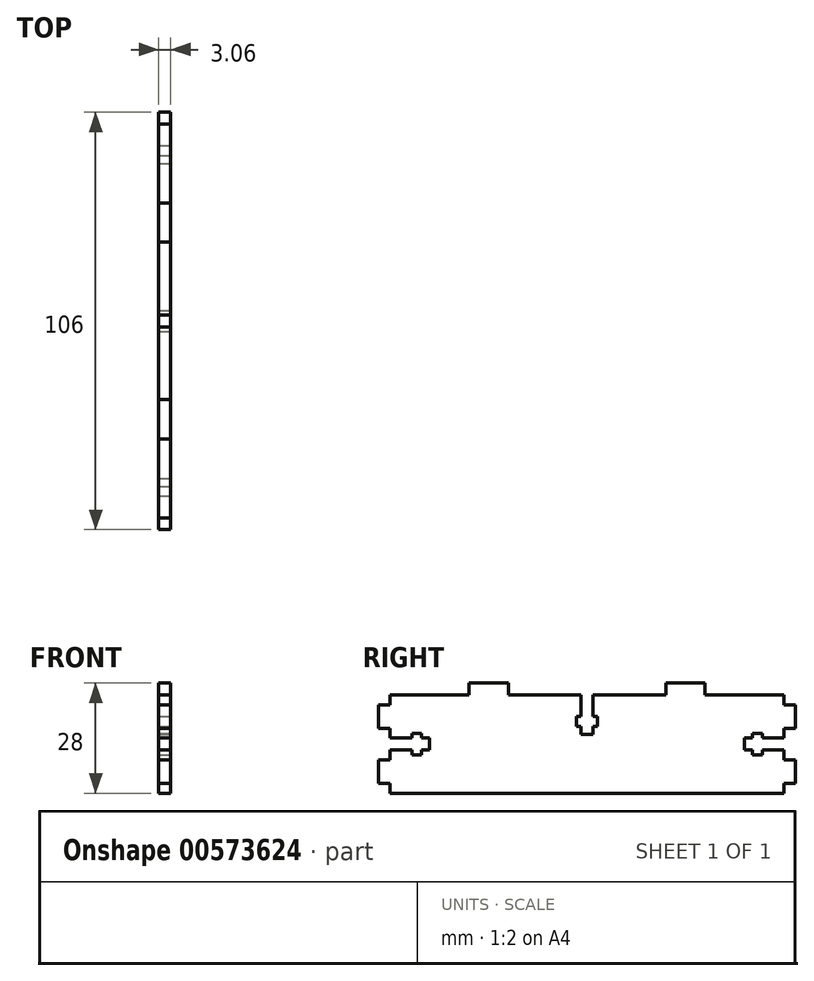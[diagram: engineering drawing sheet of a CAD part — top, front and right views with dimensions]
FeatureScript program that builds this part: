
annotation { "Feature Type Name" : "Feature", "Feature Type Description" : "" }
export const myFeature = defineFeature(function(context is Context, id is Id, definition is map)
    precondition{}
    {
        {
            var Q0;
            Q0=qCreatedBy(makeId("Right.planeOp"),FACE);
            var sketch = newSketch(context, id + "F0", { "sketchPlane" : qUnion([Q0])});
            skLineSegment(sketch, "E0.bottom", {"start": v(50, -12.5) * mm, "end": v(-50, -12.5) * mm});
            skLineSegment(sketch, "E0.top", {"start": v(50, 12.5) * mm, "end": v(-50, 12.5) * mm});
            skLineSegment(sketch, "E0.left", {"start": v(50, -12.5) * mm, "end": v(50, 12.5) * mm});
            skLineSegment(sketch, "E0.right", {"start": v(-50, -12.5) * mm, "end": v(-50, 12.5) * mm});
            skPoint(sketch, "E0.middle", {"position": v(0, 0) * mm});
            skSolve(sketch);
        }
        {
            var Q0;
            Q0 = qSketchRegion(id + "F0", true);
            extrude(context, id + "F1", {"entities" : qUnion([Q0]), "endBound" : BoundingType.SYMMETRIC, "depth" : 3.05 * mm, "offsetDistance" : 25 * mm});
        }
        {
            var Q0;
            Q0=makeQuery(id+"F1.opExtrude","CAP_FACE",FACE,{"disambiguationData":[OSD([sQuery(id+"F0.wireOp",EDGE,"E0.bottom"),sQuery(id+"F0.wireOp",EDGE,"E0.top"),sQuery(id+"F0.wireOp",EDGE,"E0.left"),sQuery(id+"F0.wireOp",EDGE,"E0.right")])],"isStart":false});
            var sketch = newSketch(context, id + "F2", { "sketchPlane" : qUnion([Q0])});
            skLineSegment(sketch, "E1", {"start": v(0, 12.5) * mm, "end": v(0, -12.5) * mm, "construction": true});
            skLineSegment(sketch, "E2", {"start": v(-50, 0) * mm, "end": v(50, 0) * mm, "construction": true});
            skLineSegment(sketch, "E3.bottom", {"start": v(-50, 10) * mm, "end": v(-53, 10) * mm});
            skLineSegment(sketch, "E3.top", {"start": v(-50, 4) * mm, "end": v(-53, 4) * mm});
            skLineSegment(sketch, "E3.left", {"start": v(-50, 10) * mm, "end": v(-50, 4) * mm});
            skLineSegment(sketch, "E3.right", {"start": v(-53, 10) * mm, "end": v(-53, 4) * mm});
            skLineSegment(sketch, "E4.MirrorCS", {"start": v(-53, -10) * mm, "end": v(-53, -4) * mm});
            skLineSegment(sketch, "E5.MirrorCS", {"start": v(-50, -10) * mm, "end": v(-50, -4) * mm});
            skLineSegment(sketch, "E6.MirrorCS", {"start": v(-50, -10) * mm, "end": v(-53, -10) * mm});
            skLineSegment(sketch, "E7.MirrorCS", {"start": v(-50, -4) * mm, "end": v(-53, -4) * mm});
            skLineSegment(sketch, "E8.MirrorCS", {"start": v(53, -10) * mm, "end": v(53, -4) * mm});
            skLineSegment(sketch, "E9.MirrorCS", {"start": v(53, 10) * mm, "end": v(53, 4) * mm});
            skLineSegment(sketch, "E10.MirrorCS", {"start": v(50, 10) * mm, "end": v(50, 4) * mm});
            skLineSegment(sketch, "E11.MirrorCS", {"start": v(50, 4) * mm, "end": v(53, 4) * mm});
            skLineSegment(sketch, "E12.MirrorCS", {"start": v(50, 10) * mm, "end": v(53, 10) * mm});
            skLineSegment(sketch, "E13.MirrorCS", {"start": v(50, -10) * mm, "end": v(50, -4) * mm});
            skLineSegment(sketch, "E14.MirrorCS", {"start": v(50, -4) * mm, "end": v(53, -4) * mm});
            skLineSegment(sketch, "E15.MirrorCS", {"start": v(50, -10) * mm, "end": v(53, -10) * mm});
            skSolve(sketch);
        }
        {
            var Q0;
            Q0 = qSketchRegion(id + "F2", true);
            var Q1;
            Q1=makeQuery(id+"F1.opExtrude","CAP_FACE",FACE,{"disambiguationData":[OSD([sQuery(id+"F0.wireOp",EDGE,"E0.bottom"),sQuery(id+"F0.wireOp",EDGE,"E0.top"),sQuery(id+"F0.wireOp",EDGE,"E0.left"),sQuery(id+"F0.wireOp",EDGE,"E0.right")])],"isStart":true});
            extrude(context, id + "F3", {"entities" : qUnion([Q0]), "operationType" : NewBodyOperationType.ADD, "endBound" : BoundingType.UP_TO_SURFACE, "oppositeDirection" : true, "depth" : 3.05 * mm, "endBoundEntityFace" : qUnion([Q1]), "offsetDistance" : 25 * mm});
        }
        {
            var Q0;
            Q0=makeQuery(id+"F3.boolean.opBoolean","MERGE",FACE,{"derivedFrom":[makeQuery(id+"F1.opExtrude","CAP_FACE",FACE,{"disambiguationData":[OSD([sQuery(id+"F0.wireOp",EDGE,"E0.bottom"),sQuery(id+"F0.wireOp",EDGE,"E0.top"),sQuery(id+"F0.wireOp",EDGE,"E0.left"),sQuery(id+"F0.wireOp",EDGE,"E0.right")])],"isStart":false}),makeQuery(id+"F3.opExtrude","CAP_FACE",FACE,{"disambiguationData":[OSD([sQuery(id+"F2.wireOp",EDGE,"E3.bottom"),sQuery(id+"F2.wireOp",EDGE,"E3.top"),sQuery(id+"F2.wireOp",EDGE,"E3.left"),sQuery(id+"F2.wireOp",EDGE,"E3.right")])],"isStart":true}),makeQuery(id+"F3.opExtrude","CAP_FACE",FACE,{"disambiguationData":[OSD([sQuery(id+"F2.wireOp",EDGE,"E4.MirrorCS"),sQuery(id+"F2.wireOp",EDGE,"E5.MirrorCS"),sQuery(id+"F2.wireOp",EDGE,"E6.MirrorCS"),sQuery(id+"F2.wireOp",EDGE,"E7.MirrorCS")])],"isStart":true}),makeQuery(id+"F3.opExtrude","CAP_FACE",FACE,{"disambiguationData":[OSD([sQuery(id+"F2.wireOp",EDGE,"E8.MirrorCS"),sQuery(id+"F2.wireOp",EDGE,"E13.MirrorCS"),sQuery(id+"F2.wireOp",EDGE,"E14.MirrorCS"),sQuery(id+"F2.wireOp",EDGE,"E15.MirrorCS")])],"isStart":true}),makeQuery(id+"F3.opExtrude","CAP_FACE",FACE,{"disambiguationData":[OSD([sQuery(id+"F2.wireOp",EDGE,"E9.MirrorCS"),sQuery(id+"F2.wireOp",EDGE,"E10.MirrorCS"),sQuery(id+"F2.wireOp",EDGE,"E11.MirrorCS"),sQuery(id+"F2.wireOp",EDGE,"E12.MirrorCS")])],"isStart":true})]});
            var sketch = newSketch(context, id + "F4", { "sketchPlane" : qUnion([Q0])});
            skLineSegment(sketch, "E16", {"start": v(-50, 0) * mm, "end": v(50, 0) * mm, "construction": true});
            skLineSegment(sketch, "E17.bottom", {"start": v(-1.55, 12.5) * mm, "end": v(1.55, 12.5) * mm});
            skLineSegment(sketch, "E17.top", {"start": v(-1.55, 2.5) * mm, "end": v(1.55, 2.5) * mm});
            skLineSegment(sketch, "E17.left", {"start": v(-1.55, 12.5) * mm, "end": v(-1.55, 2.5) * mm});
            skLineSegment(sketch, "E17.right", {"start": v(1.55, 12.5) * mm, "end": v(1.55, 2.5) * mm});
            skLineSegment(sketch, "E18", {"start": v(0, 12.5) * mm, "end": v(0, -12.5) * mm, "construction": true});
            skPoint(sketch, "E19", {"position": v(0, 2.5) * mm});
            skLineSegment(sketch, "E20", {"start": v(0, 12.5) * mm, "end": v(0, 2.5) * mm, "construction": true});
            skLineSegment(sketch, "E21.bottom", {"start": v(2.7, 4.5) * mm, "end": v(-2.7, 4.5) * mm});
            skLineSegment(sketch, "E21.top", {"start": v(2.7, 7) * mm, "end": v(-2.7, 7) * mm});
            skLineSegment(sketch, "E21.left", {"start": v(2.7, 4.5) * mm, "end": v(2.7, 7) * mm});
            skLineSegment(sketch, "E21.right", {"start": v(-2.7, 4.5) * mm, "end": v(-2.7, 7) * mm});
            skPoint(sketch, "E21.middle", {"position": v(0, 5.75) * mm});
            skLineSegment(sketch, "E22.bottom", {"start": v(-50, -1.55) * mm, "end": v(-50, 1.55) * mm});
            skLineSegment(sketch, "E22.top", {"start": v(-40, -1.55) * mm, "end": v(-40, 1.55) * mm});
            skLineSegment(sketch, "E22.left", {"start": v(-50, -1.55) * mm, "end": v(-40, -1.55) * mm});
            skLineSegment(sketch, "E22.right", {"start": v(-50, 1.55) * mm, "end": v(-40, 1.55) * mm});
            skPoint(sketch, "E23", {"position": v(-40, 0) * mm});
            skLineSegment(sketch, "E24", {"start": v(-50, 0) * mm, "end": v(-40, 0) * mm, "construction": true});
            skLineSegment(sketch, "E25.bottom", {"start": v(-42, 2.7) * mm, "end": v(-42, -2.7) * mm});
            skLineSegment(sketch, "E25.top", {"start": v(-44.5, 2.7) * mm, "end": v(-44.5, -2.7) * mm});
            skLineSegment(sketch, "E25.left", {"start": v(-42, 2.7) * mm, "end": v(-44.5, 2.7) * mm});
            skLineSegment(sketch, "E25.right", {"start": v(-42, -2.7) * mm, "end": v(-44.5, -2.7) * mm});
            skPoint(sketch, "E25.middle", {"position": v(-43.25, 0) * mm});
            skLineSegment(sketch, "E26.MirrorCS", {"start": v(44.5, 2.7) * mm, "end": v(44.5, -2.7) * mm});
            skLineSegment(sketch, "E27.MirrorCS", {"start": v(50, -1.55) * mm, "end": v(50, 1.55) * mm});
            skLineSegment(sketch, "E28.MirrorCS", {"start": v(42, 2.7) * mm, "end": v(42, -2.7) * mm});
            skLineSegment(sketch, "E29.MirrorCS", {"start": v(40, -1.55) * mm, "end": v(40, 1.55) * mm});
            skLineSegment(sketch, "E30.MirrorCS", {"start": v(50, -1.55) * mm, "end": v(40, -1.55) * mm});
            skLineSegment(sketch, "E31.MirrorCS", {"start": v(42, -2.7) * mm, "end": v(44.5, -2.7) * mm});
            skLineSegment(sketch, "E32.MirrorCS", {"start": v(50, 1.55) * mm, "end": v(40, 1.55) * mm});
            skLineSegment(sketch, "E33.MirrorCS", {"start": v(42, 2.7) * mm, "end": v(44.5, 2.7) * mm});
            skSolve(sketch);
        }
        {
            var Q0;
            Q0 = qSketchRegion(id + "F4", true);
            extrude(context, id + "F5", {"entities" : qUnion([Q0]), "operationType" : NewBodyOperationType.REMOVE, "endBound" : BoundingType.UP_TO_NEXT, "oppositeDirection" : true, "depth" : 25 * mm, "offsetDistance" : 25 * mm});
        }
        {
            var Q0;
            Q0=makeQuery(id+"F3.boolean.opBoolean","MERGE",FACE,{"derivedFrom":[makeQuery(id+"F1.opExtrude","CAP_FACE",FACE,{"disambiguationData":[OSD([sQuery(id+"F0.wireOp",EDGE,"E0.bottom"),sQuery(id+"F0.wireOp",EDGE,"E0.top"),sQuery(id+"F0.wireOp",EDGE,"E0.left"),sQuery(id+"F0.wireOp",EDGE,"E0.right")])],"isStart":false}),makeQuery(id+"F3.opExtrude","CAP_FACE",FACE,{"disambiguationData":[OSD([sQuery(id+"F2.wireOp",EDGE,"E3.bottom"),sQuery(id+"F2.wireOp",EDGE,"E3.top"),sQuery(id+"F2.wireOp",EDGE,"E3.left"),sQuery(id+"F2.wireOp",EDGE,"E3.right")])],"isStart":true}),makeQuery(id+"F3.opExtrude","CAP_FACE",FACE,{"disambiguationData":[OSD([sQuery(id+"F2.wireOp",EDGE,"E4.MirrorCS"),sQuery(id+"F2.wireOp",EDGE,"E5.MirrorCS"),sQuery(id+"F2.wireOp",EDGE,"E6.MirrorCS"),sQuery(id+"F2.wireOp",EDGE,"E7.MirrorCS")])],"isStart":true}),makeQuery(id+"F3.opExtrude","CAP_FACE",FACE,{"disambiguationData":[OSD([sQuery(id+"F2.wireOp",EDGE,"E8.MirrorCS"),sQuery(id+"F2.wireOp",EDGE,"E13.MirrorCS"),sQuery(id+"F2.wireOp",EDGE,"E14.MirrorCS"),sQuery(id+"F2.wireOp",EDGE,"E15.MirrorCS")])],"isStart":true}),makeQuery(id+"F3.opExtrude","CAP_FACE",FACE,{"disambiguationData":[OSD([sQuery(id+"F2.wireOp",EDGE,"E9.MirrorCS"),sQuery(id+"F2.wireOp",EDGE,"E10.MirrorCS"),sQuery(id+"F2.wireOp",EDGE,"E11.MirrorCS"),sQuery(id+"F2.wireOp",EDGE,"E12.MirrorCS")])],"isStart":true})]});
            var sketch = newSketch(context, id + "F6", { "sketchPlane" : qUnion([Q0])});
            skLineSegment(sketch, "E34.bottom", {"start": v(-30, 12.5) * mm, "end": v(-20, 12.5) * mm});
            skLineSegment(sketch, "E34.top", {"start": v(-30, 15.5) * mm, "end": v(-20, 15.5) * mm});
            skLineSegment(sketch, "E34.left", {"start": v(-30, 12.5) * mm, "end": v(-30, 15.5) * mm});
            skLineSegment(sketch, "E34.right", {"start": v(-20, 12.5) * mm, "end": v(-20, 15.5) * mm});
            skLineSegment(sketch, "E35", {"start": v(0, 2.5) * mm, "end": v(0, -12.5) * mm, "construction": true});
            skLineSegment(sketch, "E36.MirrorCS", {"start": v(30, 12.5) * mm, "end": v(20, 12.5) * mm});
            skLineSegment(sketch, "E37.MirrorCS", {"start": v(30, 15.5) * mm, "end": v(20, 15.5) * mm});
            skLineSegment(sketch, "E38.MirrorCS", {"start": v(20, 12.5) * mm, "end": v(20, 15.5) * mm});
            skLineSegment(sketch, "E39.MirrorCS", {"start": v(30, 12.5) * mm, "end": v(30, 15.5) * mm});
            skSolve(sketch);
        }
        {
            var Q0;
            Q0 = qSketchRegion(id + "F6", true);
            var Q1;
            {var subQ0=sQuery(id+"F0.wireOp",EDGE,"E0.right");var subQ1=sQuery(id+"F0.wireOp",EDGE,"E0.left");var subQ2=sQuery(id+"F0.wireOp",EDGE,"E0.top");var subQ3=sQuery(id+"F0.wireOp",EDGE,"E0.bottom");Q1=makeQuery(id+"F3.boolean.opBoolean","MERGE",FACE,{"derivedFrom":[makeQuery(id+"F1.opExtrude","CAP_FACE",FACE,{"disambiguationData":[OSD([subQ3,subQ2,subQ1,subQ0])],"isStart":true}),makeQuery(id+"F3.opExtrude","CAP_FACE",FACE,{"disambiguationData":[OSD([subQ3,subQ2,subQ1,subQ0]),OD(0.0)],"isStart":false}),makeQuery(id+"F3.opExtrude","CAP_FACE",FACE,{"disambiguationData":[OSD([subQ3,subQ2,subQ1,subQ0]),OD(1.0)],"isStart":false}),makeQuery(id+"F3.opExtrude","CAP_FACE",FACE,{"disambiguationData":[OSD([subQ3,subQ2,subQ1,subQ0]),OD(2.0)],"isStart":false}),makeQuery(id+"F3.opExtrude","CAP_FACE",FACE,{"disambiguationData":[OSD([subQ3,subQ2,subQ1,subQ0]),OD(3.0)],"isStart":false})]});}
            extrude(context, id + "F7", {"entities" : qUnion([Q0]), "operationType" : NewBodyOperationType.ADD, "endBound" : BoundingType.UP_TO_SURFACE, "oppositeDirection" : true, "depth" : 25 * mm, "endBoundEntityFace" : qUnion([Q1]), "offsetDistance" : 25 * mm});
        }
    });
